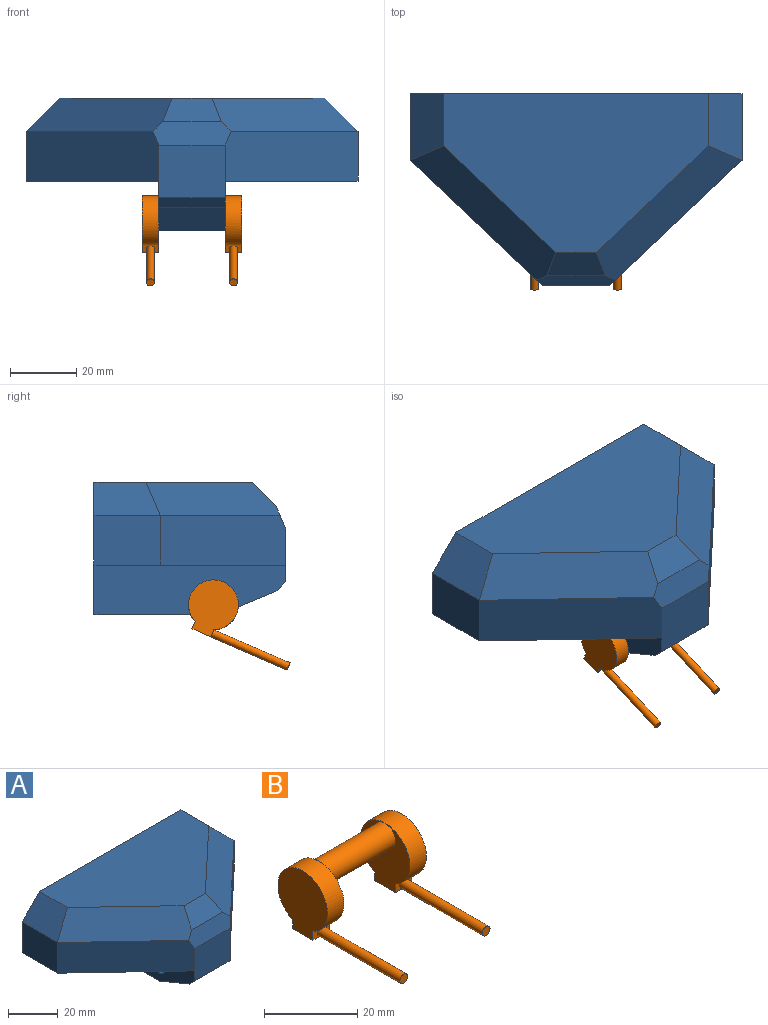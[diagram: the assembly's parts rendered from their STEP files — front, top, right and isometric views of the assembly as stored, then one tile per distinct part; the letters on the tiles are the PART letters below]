
ASSEMBLY  parts=2 mates=1
PART A: 21 faces, bbox 100x57.7x40 mm
  f0: plane 57.75x40mm, normal (0,0,-1), area 1555mm2, adj f3,f4,f5,f15
  f1: plane 40x37.75mm, normal (0.69,-0.73,0), area 819.8mm2, adj f2,f6,f8,f12,f17
  f2: plane 20x15mm, normal (1,0,0), area 300mm2, adj f1,f3,f8,f10
  f3: plane 100x40mm, normal (0,1,0), area 2700mm2, adj f0,f2,f4,f7,f8,f9,f10,f14
  f4: plane 20x15mm, normal (-1,0,0), area 300mm2, adj f0,f3,f5,f9
  f5: plane 40x37.75mm, normal (-0.69,-0.73,0), area 819.8mm2, adj f0,f4,f6,f11,f17
  f6: plane 20x15.86mm, normal (0,-1,0), area 317.2mm2, adj f1,f5,f14,f15,f17,f18
  f7: plane 80x47.75mm, normal (0,0,1), area 2730.7mm2, adj f3,f9,f10,f11,f12,f13
  f8: plane 57.75x40mm, normal (0,0,-1), area 1555mm2, adj f1,f2,f3,f14
  f9: plane 20x10mm, normal (-0.71,0,0.71), area 252.3mm2, adj f3,f4,f7,f11
  f10: plane 20x10mm, normal (0.71,0,0.71), area 252.3mm2, adj f2,f3,f7,f12
  f11: plane 43.97x40.35mm, normal (-0.49,-0.51,0.71), area 714mm2, adj f5,f7,f9,f13,f17
  f12: plane 43.97x40.35mm, normal (0.49,-0.51,0.71), area 714mm2, adj f1,f7,f10,f13,f17
  f13: plane 17.67x7.07mm, normal (0,-0.71,0.71), area 148.6mm2, adj f7,f11,f12,f17
  f14: plane 57.75x15mm, normal (1,0,0), area 750.7mm2, adj f3,f6,f8,f16,f18,f19,f20
  f15: plane 57.75x15mm, normal (-1,0,0), area 750.7mm2, adj f0,f3,f6,f16,f18,f19,f20
  f16: plane 37.75x20mm, normal (0,0,-1), area 755mm2, adj f3,f14,f15,f19
  f17: plane 23.64x7.07mm, normal (0,-0.92,0.38), area 163.3mm2, adj f1,f5,f6,f11,f12,f13
  f18: plane 20x2.93mm, normal (0,-0.71,-0.71), area 82.8mm2, adj f6,f14,f15,f19
  f19: plane 20x17.07mm, normal (0,-0.38,-0.92), area 369.6mm2, adj f14,f15,f16,f18
  f20: cylinder r=3.1mm len=20mm, axis (-1,0,0), area 389.6mm2, adj f14,f15
PART B: 19 faces, bbox 30x35.6x16.7 mm
  f0: plane 2.5x2.34mm, normal (0,-1,0), area 3.7mm2, adj f3,f5,f7,f8
  f1: cylinder r=3.1mm len=20mm, axis (-1,0,0), area 389.6mm2, adj f7,f16
  f2: plane 5x2.34mm, normal (0,1,0), area 11.7mm2, adj f3,f5,f6,f7
  f3: cylinder r=7.5mm len=15mm, axis (-1,0,0), area 203.7mm2, adj f0,f2,f4,f6,f7
  f4: plane 2.5x2.34mm, normal (0,-1,0), area 3.7mm2, adj f3,f5,f6,f8
  f5: plane 6.2x5mm, normal (0,0,-1), area 31mm2, adj f0,f2,f4,f6,f7
  f6: plane 16.67x15mm, normal (1,0,0), area 188.4mm2, adj f2,f3,f4,f5
  f7: plane 16.67x15mm, normal (-1,0,0), area 158.2mm2, adj f0,f1,f2,f3,f5
  f8: cylinder r=1.17mm len=25mm, axis (0,1,0), area 183.9mm2, adj f0,f4,f9
  f9: plane 2.34x2.34mm, normal (0,-1,0), area 4.3mm2, adj f8
  f10: plane 2.5x2.34mm, normal (0,-1,0), area 3.7mm2, adj f12,f14,f16,f17
  f11: plane 5x2.34mm, normal (0,1,0), area 11.7mm2, adj f12,f14,f15,f16
  f12: cylinder r=7.5mm len=15mm, axis (1,0,0), area 203.7mm2, adj f10,f11,f13,f15,f16
  f13: plane 2.5x2.34mm, normal (0,-1,0), area 3.7mm2, adj f12,f14,f15,f17
  f14: plane 6.2x5mm, normal (0,0,-1), area 31mm2, adj f10,f11,f13,f15,f16
  f15: plane 16.67x15mm, normal (-1,0,0), area 188.4mm2, adj f11,f12,f13,f14
  f16: plane 16.67x15mm, normal (1,0,0), area 158.2mm2, adj f1,f10,f11,f12,f14
  f17: cylinder r=1.17mm len=25mm, axis (0,1,0), area 183.9mm2, adj f10,f13,f18
  f18: plane 2.34x2.34mm, normal (0,-1,0), area 4.3mm2, adj f17
PLACE A t=(-15.59,-24.82,14.59)mm fixed
PLACE B rot(axis=(1,0,0),23.5deg) t=(-15.59,-4.82,6.66)mm
MATE revolute A.f20 <-> B.f1  axis (-1,0,0) through (-15.59,-4.82,6.66)mm
